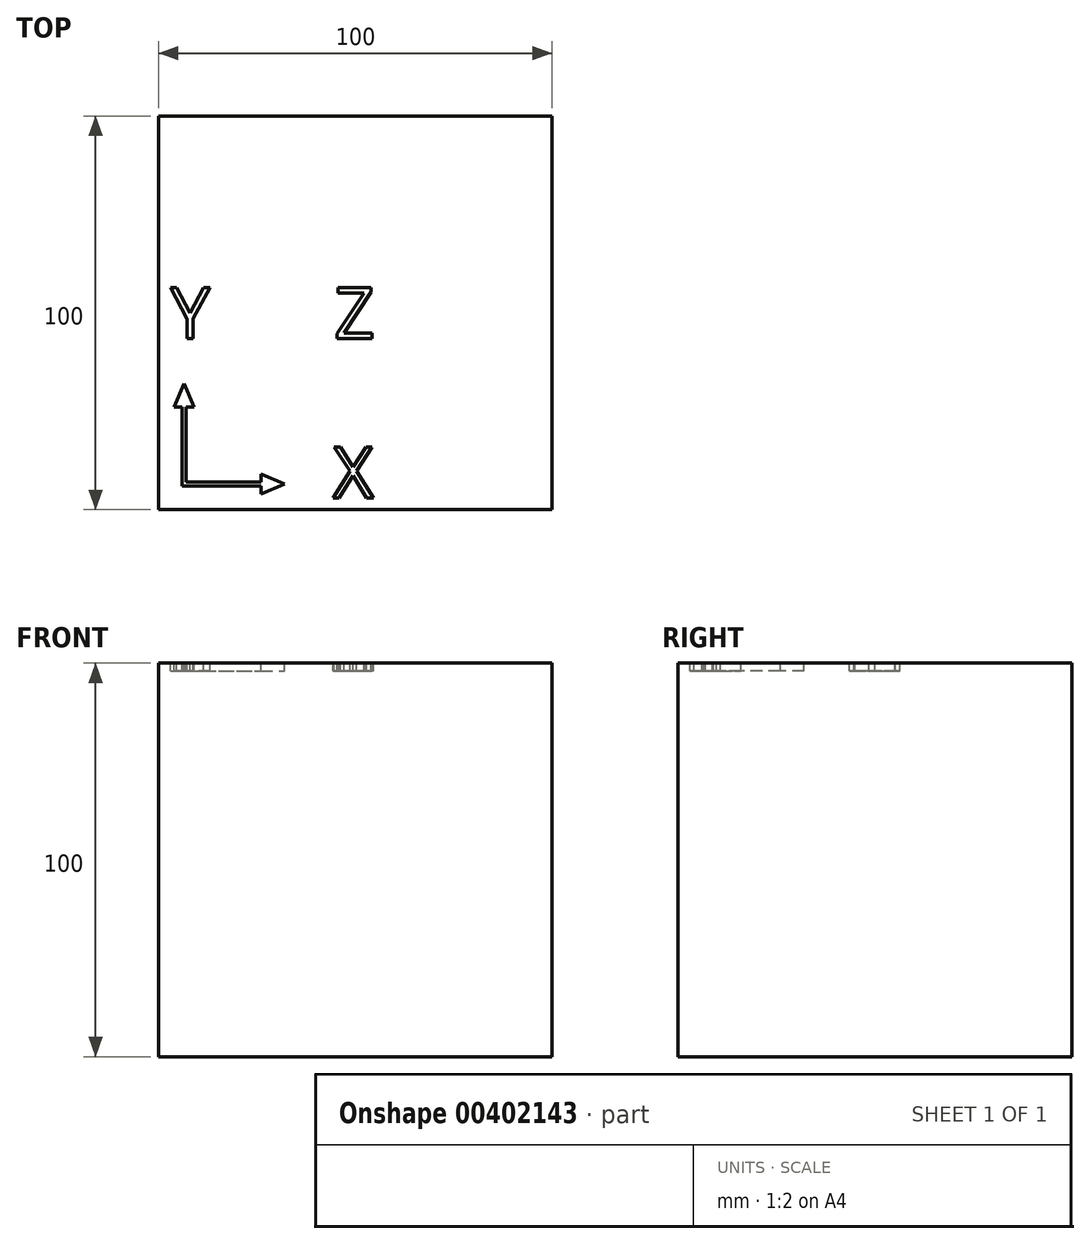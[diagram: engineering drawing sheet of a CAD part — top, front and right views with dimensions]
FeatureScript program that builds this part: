
annotation { "Feature Type Name" : "Feature", "Feature Type Description" : "" }
export const myFeature = defineFeature(function(context is Context, id is Id, definition is map)
    precondition{}
    {
        {
            var Q0;
            Q0=qCreatedBy(makeId("Top.planeOp"),FACE);
            var sketch = newSketch(context, id + "F0", { "sketchPlane" : qUnion([Q0])});
            skLineSegment(sketch, "E0.bottom", {"start": v(-61.6, 68.76) * mm, "end": v(38.4, 68.76) * mm});
            skLineSegment(sketch, "E0.top", {"start": v(-61.6, -31.24) * mm, "end": v(38.4, -31.24) * mm});
            skLineSegment(sketch, "E0.left", {"start": v(-61.6, 68.76) * mm, "end": v(-61.6, -31.24) * mm});
            skLineSegment(sketch, "E0.right", {"start": v(38.4, 68.76) * mm, "end": v(38.4, -31.24) * mm});
            skSolve(sketch);
        }
        {
            var Q0;
            Q0 = qSketchRegion(id + "F0", true);
            extrude(context, id + "F1", {"entities" : qUnion([Q0]), "depth" : 100 * mm});
        }
        {
            var Q0;
            Q0=makeQuery(id+"F1.opExtrude","CAP_FACE",FACE,{"disambiguationData":[OSD([sQuery(id+"F0.wireOp",EDGE,"E0.bottom"),sQuery(id+"F0.wireOp",EDGE,"E0.top"),sQuery(id+"F0.wireOp",EDGE,"E0.left"),sQuery(id+"F0.wireOp",EDGE,"E0.right")])],"isStart":false});
            var sketch = newSketch(context, id + "F2", { "sketchPlane" : qUnion([Q0])});
            skText(sketch, "E1", { "text": "X", "fontName": "OpenSans-Regular.ttf"});
            skText(sketch, "E2", { "text": "Y", "fontName": "OpenSans-Regular.ttf"});
            skPoint(sketch, "E3", {"position": v(-58.6, 18.76) * mm});
            skPoint(sketch, "E4", {"position": v(-61.6, 18.76) * mm});
            skText(sketch, "E5", { "text": "Z", "fontName": "OpenSans-Regular.ttf"});
            skPoint(sketch, "E6", {"position": v(-11.6, 18.76) * mm});
            skLineSegment(sketch, "E7.top", {"start": v(-55.6, -25.24) * mm, "end": v(-35.6, -25.24) * mm});
            skLineSegment(sketch, "E7.left", {"start": v(-55.6, -5.24) * mm, "end": v(-55.6, -25.24) * mm});
            skLineSegment(sketch, "E8.0", {"start": v(-54.6, -24.24) * mm, "end": v(-35.6, -24.24) * mm});
            skLineSegment(sketch, "E8.1", {"start": v(-54.6, -5.24) * mm, "end": v(-54.6, -24.24) * mm});
            skLineSegment(sketch, "E9", {"start": v(-55.6, -5.24) * mm, "end": v(-57.6, -5.24) * mm});
            skLineSegment(sketch, "E10", {"start": v(-57.6, -5.24) * mm, "end": v(-55.1, 0.76) * mm});
            skLineSegment(sketch, "E11", {"start": v(-55.1, 0.76) * mm, "end": v(-52.6, -5.24) * mm});
            skLineSegment(sketch, "E12", {"start": v(-52.6, -5.24) * mm, "end": v(-54.6, -5.24) * mm});
            skLineSegment(sketch, "E13", {"start": v(-35.6, -25.24) * mm, "end": v(-35.6, -27.24) * mm});
            skLineSegment(sketch, "E14", {"start": v(-35.6, -27.24) * mm, "end": v(-29.6, -24.74) * mm});
            skLineSegment(sketch, "E15", {"start": v(-29.6, -24.74) * mm, "end": v(-35.6, -22.24) * mm});
            skLineSegment(sketch, "E16", {"start": v(-35.6, -22.24) * mm, "end": v(-35.6, -24.24) * mm});
            const initialGuessF2  = {"E1": [-0.01736, -0.02824, 1, 0, 0.013], "E2": [-0.0586, 0.01226, 1, 0, 0.013], "E5": [-0.01698, 0.01226, 1, 0, 0.013]};
            skSetInitialGuess(sketch, initialGuessF2);
            skSolve(sketch);
        }
        {
            var Q0;
            Q0 = qSketchRegion(id + "F2", true);
            extrude(context, id + "F3", {"entities" : qUnion([Q0]), "operationType" : NewBodyOperationType.REMOVE, "oppositeDirection" : true, "depth" : 2 * mm});
        }
    });
